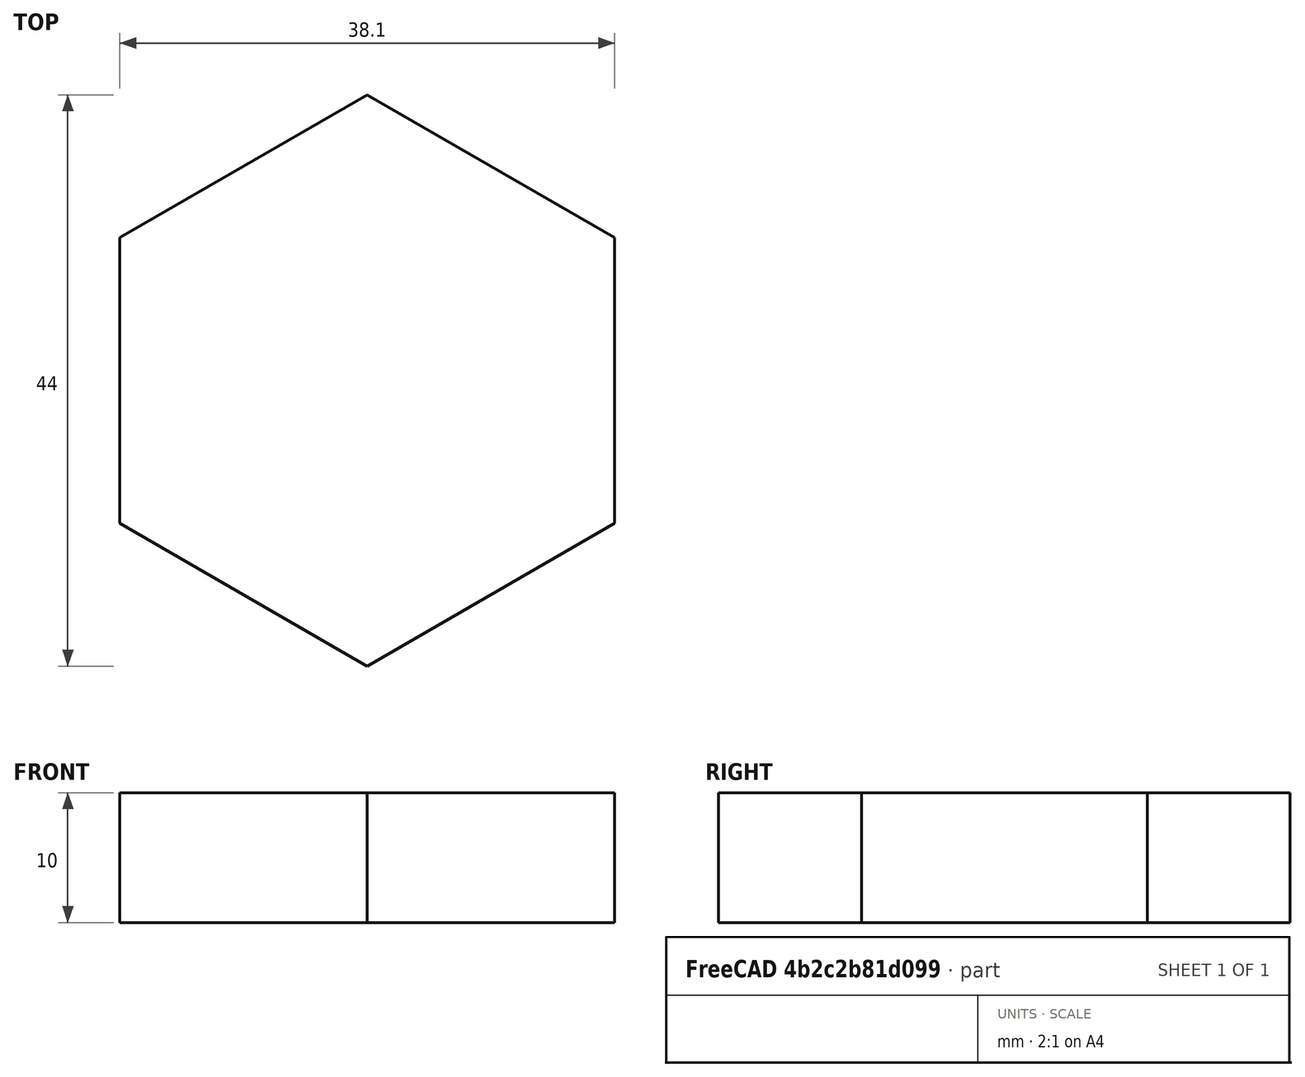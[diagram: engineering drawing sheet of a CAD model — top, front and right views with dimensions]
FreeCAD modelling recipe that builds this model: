
FCSTD DOCUMENT  (FreeCAD 0.21R33668 +26 (Git))
Label: Ressort-essai3
License: All rights reserved
LicenseURL: http://en.wikipedia.org/wiki/All_rights_reserved
objects: Sketcher::SketchObject×2, Part::Helix×1, PartDesign::FeatureBase×1, PartDesign::Pad×1, PartDesign::Body×1
note: 7 computed .brp shape members not serialized (recipe doc carries the construction recipe); baked Part::Feature solids carry a one-line shape summary decoded from their .brp

FEATURE [Sketcher::SketchObject] Sketch
  FullyConstrained = true
  MapMode = 5
  Support = -> [XY_Plane]
  sketch-geometry (7):
    g0: LineSegment StartX=19.0526 StartY=11 StartZ=0 EndX=0 EndY=22 EndZ=0
    g1: LineSegment StartX=0 StartY=22 StartZ=0 EndX=-19.0526 EndY=11 EndZ=0
    g2: LineSegment StartX=-19.0526 StartY=11 StartZ=0 EndX=-19.0526 EndY=-11 EndZ=0
    g3: LineSegment StartX=-19.0526 StartY=-11 StartZ=0 EndX=3.6e-15 EndY=-22 EndZ=0
    g4: LineSegment StartX=3.6e-15 StartY=-22 StartZ=0 EndX=19.0526 EndY=-11 EndZ=0
    g5: LineSegment StartX=19.0526 StartY=-11 StartZ=0 EndX=19.0526 EndY=11 EndZ=0
    g6: Circle CenterX=0 CenterY=0 CenterZ=0 NormalX=0 NormalY=0 NormalZ=1 AngleXU=0 Radius=22
  constraints (16):
    c: Coincident(g0,g1)
    c: Coincident(g1,g2)
    c: Coincident(g2,g3)
    c: Coincident(g3,g4)
    c: Coincident(g4,g5)
    c: Coincident(g5,g0)
    c: Equal(g0, g1-g5) x5
    c: PointOnObject(g0,g6)
    c: PointOnObject(g1,g6)
    c: PointOnObject(g2,g6)
    c: PointOnObject(g3,g6)
    c: PointOnObject(g4,g6)
    c: PointOnObject(g5,g6)
    c: Coincident(g6,g-1)
    c: PointOnObject(g0,g-2)
    c: DistanceY(g6,g0) = 22
FEATURE [Part::Helix] Helix  label="Hélice"
  Angle = 0
  AttacherType = Attacher::AttachEngine3D
  Height = 200
  LocalCoord = 0
  Pitch = 20
  Radius = 16
  SegmentLength = 0
  Style = 1
FEATURE [Sketcher::SketchObject] Sketch001
  FullyConstrained = true
  MapMode = 5
  Placement = pos=(0,0,0) rot=(1,0,0;1.5708rad)
  Support = -> [XZ_Plane]
  sketch-geometry (1):
    g0: Circle CenterX=15 CenterY=0 CenterZ=0 NormalX=0 NormalY=0 NormalZ=1 AngleXU=0 Radius=4
  constraints (3):
    c: PointOnObject(g0,g-1)
    c: Radius(g0) = 4
    c: DistanceX(g-1,g0) = 15
FEATURE [PartDesign::FeatureBase] BaseFeature
  BaseFeature = -> Helix
FEATURE [PartDesign::Pad] Pad
  BaseFeature = -> BaseFeature
  Direction = (0,0,1)
  Length = 10
  Length2 = 10
  Profile = -> Sketch
  ReferenceAxis = -> Sketch [N_Axis]
  Type = 0
FEATURE [PartDesign::Body] Body  label="Corps"
  BaseFeature = -> Helix
  Group = -> [BaseFeature,Sketch,Pad,Sketch001]
  Origin = -> Origin
  Tip = -> Pad
